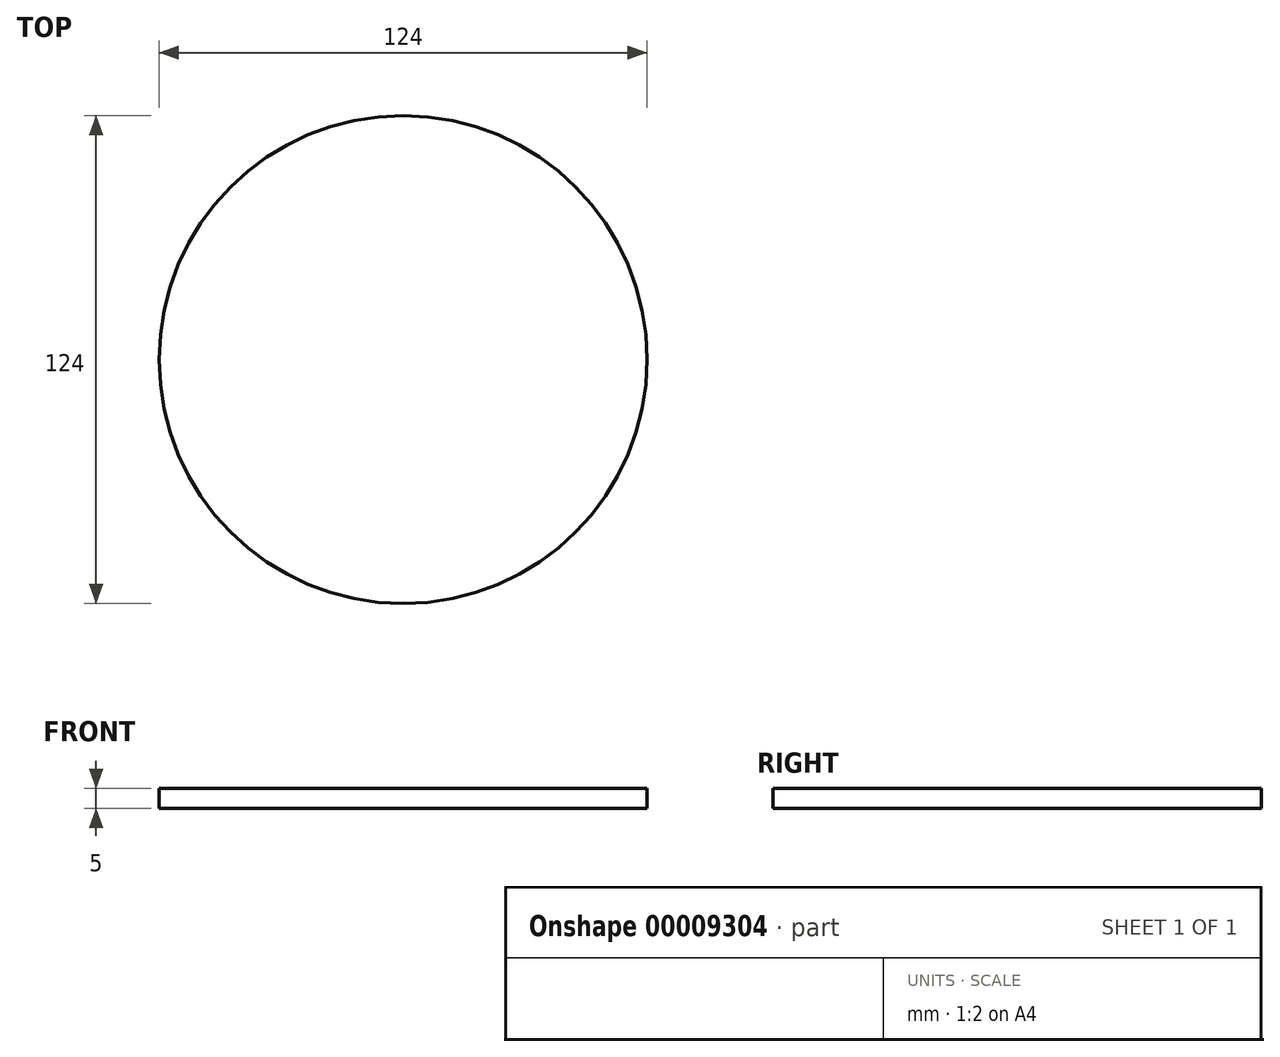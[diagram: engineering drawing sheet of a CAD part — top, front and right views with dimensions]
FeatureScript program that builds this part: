
annotation { "Feature Type Name" : "Feature", "Feature Type Description" : "" }
export const myFeature = defineFeature(function(context is Context, id is Id, definition is map)
    precondition{}
    {
        {
            var Q0;
            Q0=qCreatedBy(makeId("Top.planeOp"),FACE);
            var sketch = newSketch(context, id + "F0", { "sketchPlane" : qUnion([Q0])});
            skCircle(sketch, "E0", {"center": v(0, 0) * mm, "radius": 60 * mm, "construction": true});
            skCircle(sketch, "E1", {"center": v(-42.69, 42.16) * mm, "radius": 2 * mm});
            skCircle(sketch, "E2.1.0", {"center": v(-59.32, 9.02) * mm, "radius": 2 * mm});
            skCircle(sketch, "E2.2.0", {"center": v(-53.3, -27.57) * mm, "radius": 2 * mm});
            skCircle(sketch, "E2.3.0", {"center": v(-26.9, -53.63) * mm, "radius": 2 * mm});
            skCircle(sketch, "E2.4.0", {"center": v(9.75, -59.2) * mm, "radius": 2 * mm});
            skCircle(sketch, "E2.5.0", {"center": v(42.69, -42.16) * mm, "radius": 2 * mm});
            skCircle(sketch, "E2.6.0", {"center": v(59.32, -9.02) * mm, "radius": 2 * mm});
            skCircle(sketch, "E2.7.0", {"center": v(53.3, 27.57) * mm, "radius": 2 * mm});
            skCircle(sketch, "E2.8.0", {"center": v(26.9, 53.63) * mm, "radius": 2 * mm});
            skCircle(sketch, "E2.9.0", {"center": v(-9.75, 59.2) * mm, "radius": 2 * mm});
            skCircle(sketch, "E3", {"center": v(0, 0) * mm, "radius": 62 * mm});
            skSolve(sketch);
        }
        {
            var Q0;
            Q0 = qSketchRegion(id + "F0", true);
            extrude(context, id + "F1", {"entities" : qUnion([Q0]), "oppositeDirection" : true, "depth" : 5 * mm});
        }
    });
